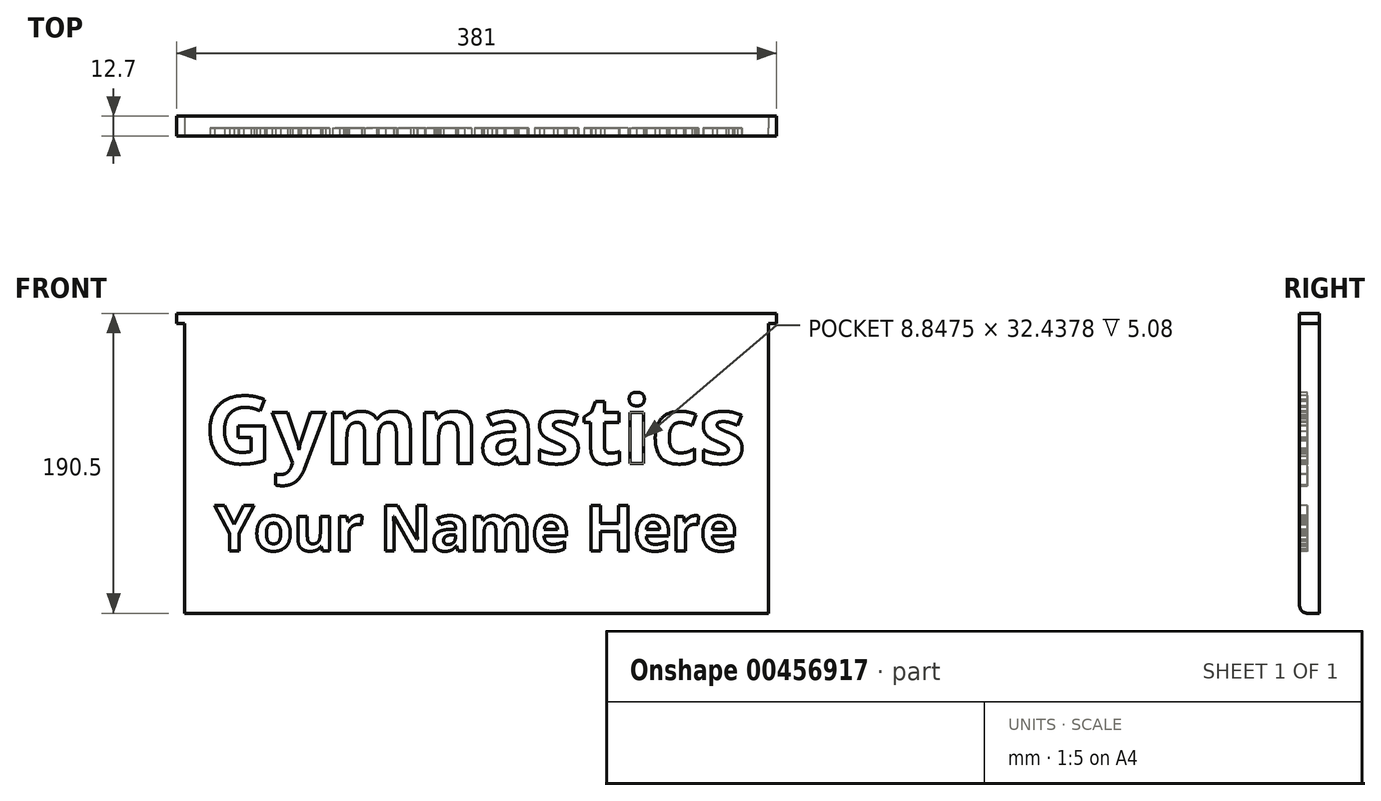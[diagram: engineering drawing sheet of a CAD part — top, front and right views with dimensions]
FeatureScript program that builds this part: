
annotation { "Feature Type Name" : "Feature", "Feature Type Description" : "" }
export const myFeature = defineFeature(function(context is Context, id is Id, definition is map)
    precondition{}
    {
        {
            var Q0;
            Q0=qCreatedBy(makeId("Front.planeOp"),FACE);
            var sketch = newSketch(context, id + "F0", { "sketchPlane" : qUnion([Q0])});
            skLineSegment(sketch, "E0.bottom", {"start": v(-190.5, 95.25) * mm, "end": v(190.5, 95.25) * mm});
            skLineSegment(sketch, "E0.top", {"start": v(-190.5, -95.25) * mm, "end": v(190.5, -95.25) * mm});
            skLineSegment(sketch, "E0.left", {"start": v(-190.5, 95.25) * mm, "end": v(-190.5, -95.25) * mm});
            skLineSegment(sketch, "E0.right", {"start": v(190.5, 95.25) * mm, "end": v(190.5, -95.25) * mm});
            skPoint(sketch, "E0.middle", {"position": v(0, 0) * mm});
            skSolve(sketch);
        }
        {
            var Q0;
            Q0=makeQuery(id+"F0.imprint","IMPRINT",FACE,{"disambiguationData":[TD([[makeQuery(id+"F0.imprint","IMPRINT",EDGE,{"derivedFrom":sQuery(id+"F0.wireOp",EDGE,"E0.bottom")}),-1.0]])]});
            extrude(context, id + "F1", {"entities" : qUnion([Q0]), "depth" : 12.7 * mm});
        }
        {
            var Q0;
            Q0=makeQuery(id+"F1.opExtrude","CAP_FACE",FACE,{"disambiguationData":[OSD([sQuery(id+"F0.wireOp",EDGE,"E0.bottom"),sQuery(id+"F0.wireOp",EDGE,"E0.top"),sQuery(id+"F0.wireOp",EDGE,"E0.left"),sQuery(id+"F0.wireOp",EDGE,"E0.right")])],"isStart":false});
            var sketch = newSketch(context, id + "F2", { "sketchPlane" : qUnion([Q0])});
            skText(sketch, "E1", { "text": "Gymnastics", "fontName": "OpenSans-Bold.ttf"});
            skText(sketch, "E2", { "text": "Your Name Here", "fontName": "OpenSans-Bold.ttf"});
            const initialGuessF2  = {"E1": [-0.17278, 0, 1, 0, 0.04278], "E2": [-0.16647, -0.05555, 1, 0, 0.02893]};
            skSetInitialGuess(sketch, initialGuessF2);
            skSolve(sketch);
        }
        {
            var Q0;
            Q0=qSketchRegion(id+"F2",true);
            extrude(context, id + "F3", {"entities" : qUnion([Q0]), "operationType" : NewBodyOperationType.REMOVE, "oppositeDirection" : true, "depth" : 5.08 * mm});
        }
        {
            var Q0;
            {var subQ0=sQuery(id+"F0.wireOp",EDGE,"E0.left");var subQ1=sQuery(id+"F0.wireOp",EDGE,"E0.bottom");var subQ2=sQuery(id+"F0.wireOp",EDGE,"E0.right");var subQ3=sQuery(id+"F0.wireOp",EDGE,"E0.top");Q0=makeQuery(id+"F3.boolean.opBoolean","SPLIT",FACE,{"disambiguationData":[TD([makeQuery(id+"F1.opExtrude","SWEPT_FACE",FACE,{"disambiguationData":[OSD([subQ1])]})])],"derivedFrom":makeQuery(id+"F1.opExtrude","CAP_FACE",FACE,{"disambiguationData":[OSD([subQ1,subQ3,subQ0,subQ2])],"isStart":false})});}
            var sketch = newSketch(context, id + "F4", { "sketchPlane" : qUnion([Q0])});
            skPoint(sketch, "E3", {"position": v(-185.42, 95.25) * mm});
            skPoint(sketch, "E4", {"position": v(-185.42, -95.25) * mm});
            skPoint(sketch, "E5", {"position": v(185.42, 95.25) * mm});
            skPoint(sketch, "E6", {"position": v(190.5, 88.9) * mm});
            skPoint(sketch, "E7", {"position": v(185.42, -95.25) * mm});
            skPoint(sketch, "E8", {"position": v(-190.5, 88.9) * mm});
            skLineSegment(sketch, "E9", {"start": v(-185.42, 95.25) * mm, "end": v(-185.42, -95.25) * mm});
            skLineSegment(sketch, "E10", {"start": v(-190.5, 88.9) * mm, "end": v(-185.42, 88.9) * mm});
            skLineSegment(sketch, "E11", {"start": v(185.42, -95.25) * mm, "end": v(185.42, 95.25) * mm});
            skLineSegment(sketch, "E12", {"start": v(190.5, 88.9) * mm, "end": v(185.42, 88.9) * mm});
            skPoint(sketch, "E13", {"position": v(-32.37, -40.44) * mm});
            skPoint(sketch, "E14", {"position": v(-37.84, -40.44) * mm});
            skSolve(sketch);
        }
        {
            var Q0;
            {var subQ3=sQuery(id+"F4.wireOp",EDGE,"E10");Q0=makeQuery(id+"F4.imprint","IMPRINT",FACE,{"disambiguationData":[TD([[makeQuery(id+"F4.imprint","IMPRINT",EDGE,{"derivedFrom":subQ3}),-1.0]])]});}
            var Q1;
            {var subQ3=sQuery(id+"F4.wireOp",EDGE,"E12");Q1=makeQuery(id+"F4.imprint","IMPRINT",FACE,{"disambiguationData":[TD([[makeQuery(id+"F4.imprint","IMPRINT",EDGE,{"derivedFrom":subQ3}),1.0]])]});}
            extrude(context, id + "F5", {"entities" : qUnion([Q0, Q1]), "operationType" : NewBodyOperationType.REMOVE, "oppositeDirection" : true, "depth" : 12.7 * mm});
        }
        {
            var Q0;
            Q0=makeQuery(id+"F1.opExtrude","CAP_EDGE",EDGE,{"disambiguationData":[OSD([sQuery(id+"F0.wireOp",EDGE,"E0.top")])],"isStart":false});
            var Q1;
            Q1=makeQuery(id+"F5.boolean.opBoolean","COPY",EDGE,{"derivedFrom":makeQuery(id+"F5.opExtrude","CAP_EDGE",EDGE,{"disambiguationData":[OSD([sQuery(id+"F4.wireOp",EDGE,"E11")])],"isStart":true})});
            var Q2;
            Q2=makeQuery(id+"F5.boolean.opBoolean","COPY",EDGE,{"derivedFrom":makeQuery(id+"F5.opExtrude","CAP_EDGE",EDGE,{"disambiguationData":[OSD([sQuery(id+"F4.wireOp",EDGE,"E9")])],"isStart":true})});
            fillet(context, id + "F6", {"entities" : qUnion([Q0, Q1, Q2]), "radius" : 5.08 * mm, "tangentPropagation" : true, "allowEdgeOverflow" : false});
        }
    });
